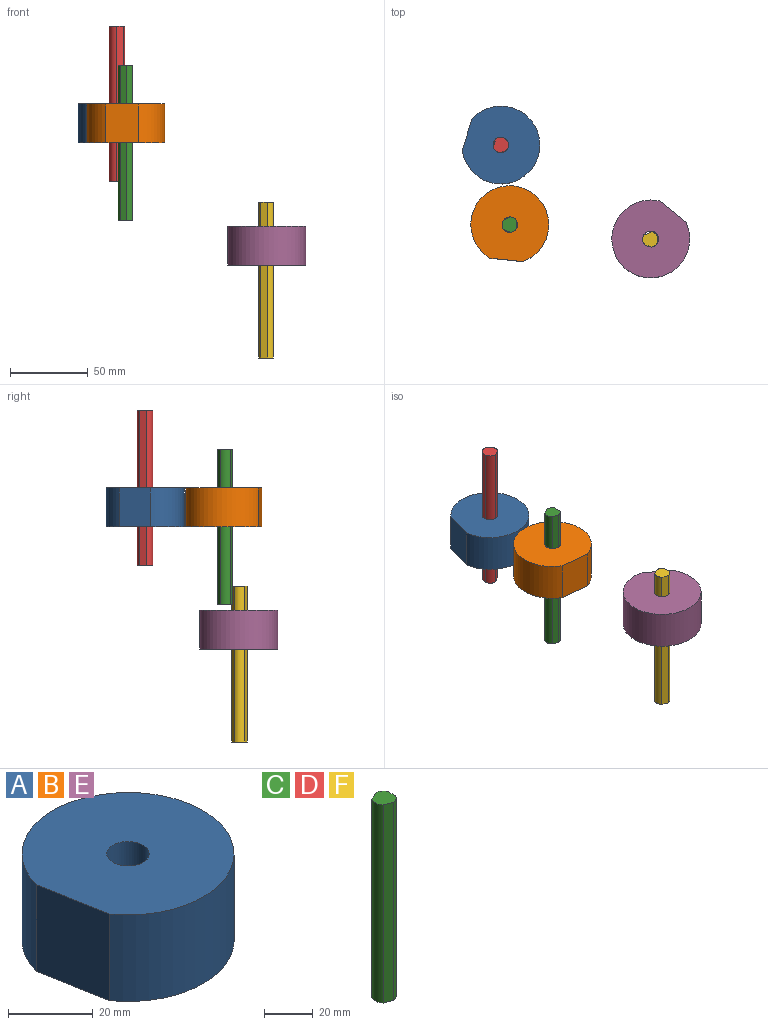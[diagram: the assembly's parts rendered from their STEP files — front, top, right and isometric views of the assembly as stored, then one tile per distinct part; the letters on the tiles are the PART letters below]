
ASSEMBLY  parts=6 mates=3
PART A: 5 faces, bbox 49.2x50x25 mm
  f0: cylinder r=25mm len=50mm, axis (0,0,-1), area 3386mm2, adj f2,f3,f4
  f1: cylinder r=5mm len=25mm, axis (0,0,-1), area 785.4mm2, adj f3,f4
  f2: plane 25x20.64mm, normal (-0.98,-0.18,0), area 524.2mm2, adj f0,f3,f4
  f3: plane 50x49.2mm, normal (0,0,1), area 1852.4mm2, adj f0,f1,f2
  f4: plane 50x49.2mm, normal (0,0,-1), area 1852.4mm2, adj f0,f1,f2
PART B: same geometry as A
PART C: 8 faces, bbox 9.5x9.9x100 mm
  f0: cylinder r=5mm len=100mm, axis (0,0,-1), area 476.7mm2, adj f1,f5,f6,f7
  f1: plane 100x4.54mm, normal (1,0,0), area 454.1mm2, adj f0,f2,f6,f7
  f2: cylinder r=5mm len=100mm, axis (0,0,-1), area 493.5mm2, adj f1,f3,f6,f7
  f3: plane 100x4.67mm, normal (-0.41,0.91,0), area 512.5mm2, adj f2,f4,f6,f7
  f4: cylinder r=5mm len=100mm, axis (0,0,-1), area 677.7mm2, adj f3,f5,f6,f7
  f5: plane 100x4.39mm, normal (-0.33,-0.94,0), area 465.5mm2, adj f0,f4,f6,f7
  f6: plane 9.92x9.45mm, normal (0,0,1), area 72.6mm2, adj f0,f1,f2,f3,f4,f5
  f7: plane 9.92x9.45mm, normal (0,0,-1), area 72.6mm2, adj f0,f1,f2,f3,f4,f5
PART D: same geometry as C
PART E: same geometry as A
PART F: same geometry as C
PLACE A rot(axis=(0,0,-1),27.5deg) t=(-6.25,26.08,12.72)mm
PLACE B rot(axis=(0,0,1),73.9deg) t=(-24.64,-56.39,12.68)mm
PLACE C t=(-23.3,-99.92,-37.32)mm fixed
PLACE D rot(axis=(0,0,1),46.4deg) t=(13.96,-50.51,-12.28)mm fixed
PLACE E rot(axis=(0,0,-1),139.4deg) t=(114.66,-68.41,-65.71)mm
PLACE F t=(66.92,-109.23,-125.4)mm fixed
MATE cylindrical F.f0 <-> E.f3  axis (0,0,-1) through (90.45,-59.91,-75.4)mm
MATE revolute D.f0 <-> A.f0  axis (0,0,-1) through (-5.5,0.56,37.72)mm
MATE revolute C.f0 <-> B.f0  axis (0,0,-1) through (0.22,-50.59,12.68)mm
